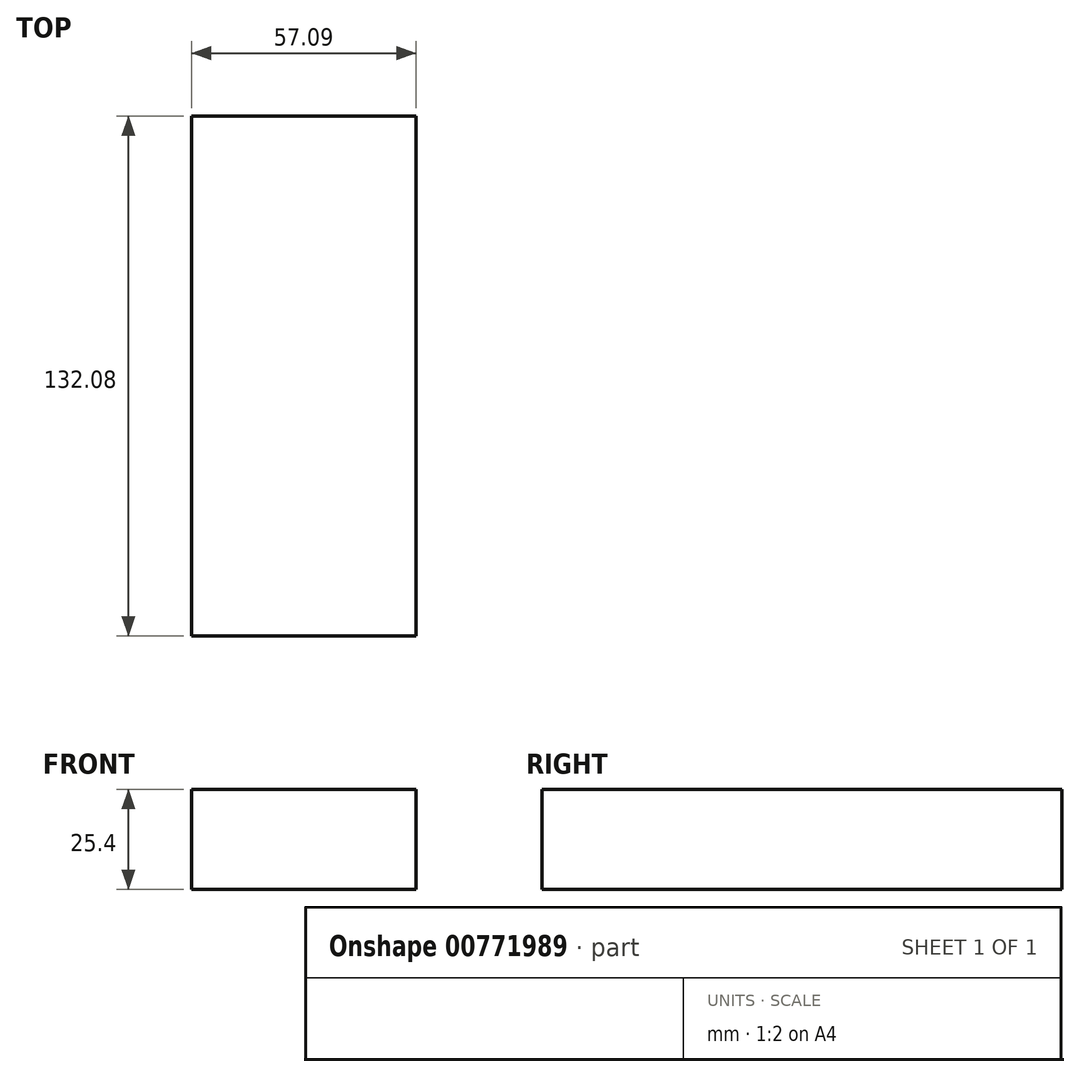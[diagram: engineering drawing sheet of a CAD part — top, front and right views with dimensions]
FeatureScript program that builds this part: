
annotation { "Feature Type Name" : "Feature", "Feature Type Description" : "" }
export const myFeature = defineFeature(function(context is Context, id is Id, definition is map)
    precondition{}
    {
        {
            var Q0;
            Q0=qCreatedBy(makeId("Top.planeOp"),FACE);
            var sketch = newSketch(context, id + "F0", { "sketchPlane" : qUnion([Q0])});
            skLineSegment(sketch, "E0.bottom", {"start": v(0, 0) * mm, "end": v(-57.09, 0) * mm});
            skLineSegment(sketch, "E0.top", {"start": v(0, 132.08) * mm, "end": v(-57.09, 132.08) * mm});
            skLineSegment(sketch, "E0.left", {"start": v(0, 0) * mm, "end": v(0, 132.08) * mm});
            skLineSegment(sketch, "E0.right", {"start": v(-57.09, 0) * mm, "end": v(-57.09, 132.08) * mm});
            skSolve(sketch);
        }
        {
            var Q0;
            Q0=makeQuery(id+"F0.imprint","IMPRINT",FACE,{"disambiguationData":[TD([[makeQuery(id+"F0.imprint","IMPRINT",EDGE,{"derivedFrom":sQuery(id+"F0.wireOp",EDGE,"E0.bottom")}),-1.0]])]});
            extrude(context, id + "F1", {"entities" : qUnion([Q0]), "depth" : 25.4 * mm, "offsetDistance" : 25.4 * mm});
        }
    });
